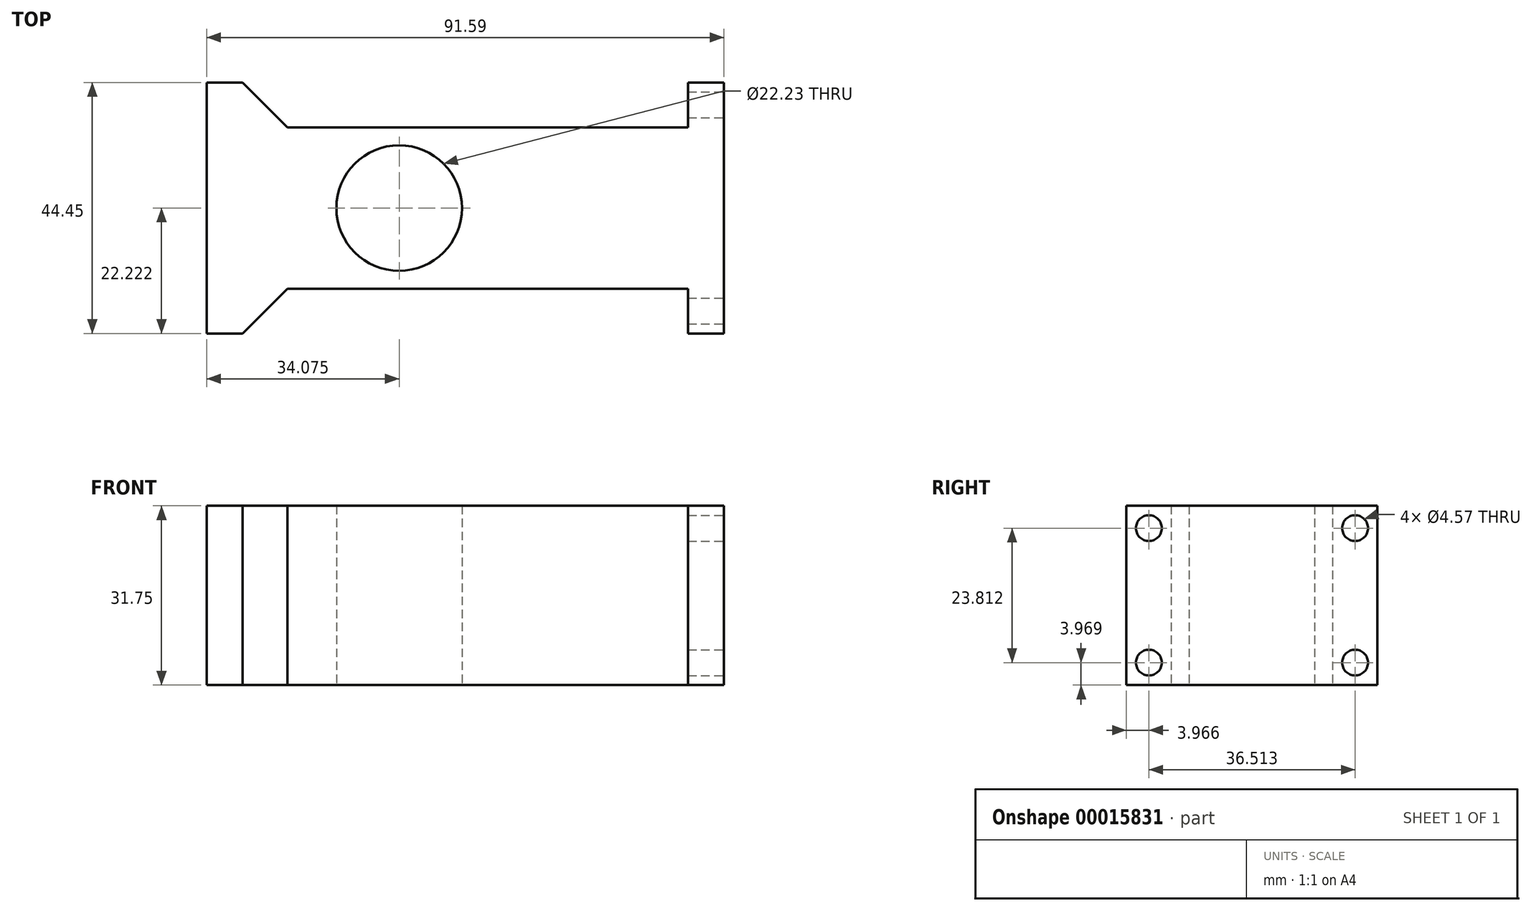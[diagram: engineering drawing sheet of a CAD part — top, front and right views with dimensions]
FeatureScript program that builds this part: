
annotation { "Feature Type Name" : "Feature", "Feature Type Description" : "" }
export const myFeature = defineFeature(function(context is Context, id is Id, definition is map)
    precondition{}
    {
        {
            var Q0;
            Q0=qCreatedBy(makeId("Top.planeOp"),FACE);
            var sketch = newSketch(context, id + "F0", { "sketchPlane" : qUnion([Q0])});
            skLineSegment(sketch, "E0.bottom", {"start": v(0, 0) * mm, "end": v(-78.9, 0) * mm});
            skLineSegment(sketch, "E0.top", {"start": v(0, -28.58) * mm, "end": v(-78.9, -28.58) * mm});
            skLineSegment(sketch, "E1.bottom", {"start": v(0, 0) * mm, "end": v(6.35, 0) * mm, "construction": true});
            skLineSegment(sketch, "E1.top", {"start": v(0, 7.94) * mm, "end": v(6.35, 7.94) * mm});
            skLineSegment(sketch, "E1.left", {"start": v(0, 0) * mm, "end": v(0, 7.94) * mm});
            skLineSegment(sketch, "E1.right", {"start": v(6.35, 0) * mm, "end": v(6.35, 7.94) * mm});
            skLineSegment(sketch, "E2.bottom", {"start": v(0, -28.58) * mm, "end": v(6.35, -28.58) * mm});
            skLineSegment(sketch, "E2.top", {"start": v(0, -36.51) * mm, "end": v(6.35, -36.51) * mm});
            skLineSegment(sketch, "E2.left", {"start": v(0, -28.58) * mm, "end": v(0, -36.51) * mm});
            skLineSegment(sketch, "E2.right", {"start": v(6.35, -28.58) * mm, "end": v(6.35, -36.51) * mm});
            skLineSegment(sketch, "E3", {"start": v(6.35, 0) * mm, "end": v(6.35, -28.58) * mm});
            skCircle(sketch, "E4", {"center": v(-51.16, -14.29) * mm, "radius": 11.11 * mm});
            skLineSegment(sketch, "E5", {"start": v(-51.16, -14.29) * mm, "end": v(-85.24, -14.29) * mm});
            skLineSegment(sketch, "E6.bottom", {"start": v(-78.9, -28.58) * mm, "end": v(-85.24, -28.58) * mm, "construction": true});
            skLineSegment(sketch, "E6.top", {"start": v(-78.9, -36.51) * mm, "end": v(-85.24, -36.51) * mm});
            skLineSegment(sketch, "E6.left", {"start": v(-78.9, -28.58) * mm, "end": v(-78.9, -36.51) * mm});
            skLineSegment(sketch, "E6.right", {"start": v(-85.24, -28.58) * mm, "end": v(-85.24, -36.51) * mm});
            skLineSegment(sketch, "E7.bottom", {"start": v(-78.9, 0) * mm, "end": v(-85.24, 0) * mm, "construction": true});
            skLineSegment(sketch, "E7.top", {"start": v(-78.9, 7.94) * mm, "end": v(-85.24, 7.94) * mm});
            skLineSegment(sketch, "E7.left", {"start": v(-78.9, 0) * mm, "end": v(-78.9, 7.94) * mm});
            skLineSegment(sketch, "E7.right", {"start": v(-85.24, 0) * mm, "end": v(-85.24, 7.94) * mm});
            skLineSegment(sketch, "E8", {"start": v(-85.24, 0) * mm, "end": v(-85.24, -28.58) * mm});
            skSolve(sketch);
        }
        {
            var Q0;
            Q0 = qSketchRegion(id + "F0", true);
            extrude(context, id + "F1", {"entities" : qUnion([Q0]), "depth" : 31.75 * mm});
        }
        {
            var Q0;
            Q0=makeQuery(id+"F1.opExtrude","SWEPT_FACE",FACE,{"disambiguationData":[OSD([sQuery(id+"F0.wireOp",EDGE,"E1.right"),sQuery(id+"F0.wireOp",EDGE,"E2.right"),sQuery(id+"F0.wireOp",EDGE,"E3")])]});
            var sketch = newSketch(context, id + "F2", { "sketchPlane" : qUnion([Q0])});
            skLineSegment(sketch, "E9", {"start": v(-32.54, 31.75) * mm, "end": v(-32.54, 27.78) * mm});
            skLineSegment(sketch, "E10", {"start": v(3.97, 31.75) * mm, "end": v(3.97, 27.78) * mm});
            skLineSegment(sketch, "E11", {"start": v(3.97, 0) * mm, "end": v(3.97, 3.97) * mm});
            skLineSegment(sketch, "E12", {"start": v(-32.54, 0) * mm, "end": v(-32.54, 3.97) * mm});
            skCircle(sketch, "E13", {"center": v(-32.54, 27.78) * mm, "radius": 2.29 * mm});
            skCircle(sketch, "E14", {"center": v(-32.54, 3.97) * mm, "radius": 2.29 * mm});
            skCircle(sketch, "E15", {"center": v(3.97, 3.97) * mm, "radius": 2.29 * mm});
            skCircle(sketch, "E16", {"center": v(3.97, 27.78) * mm, "radius": 2.29 * mm});
            skSolve(sketch);
        }
        {
            var Q0;
            Q0 = qSketchRegion(id + "F2", true);
            var Q1;
            Q1=makeQuery(id+"F1.opExtrude","SWEPT_FACE",FACE,{"disambiguationData":[OSD([sQuery(id+"F0.wireOp",EDGE,"E1.left")])]});
            extrude(context, id + "F3", {"entities" : qUnion([Q0]), "operationType" : NewBodyOperationType.REMOVE, "endBound" : BoundingType.UP_TO_SURFACE, "oppositeDirection" : true, "endBoundEntityFace" : qUnion([Q1]), "depth" : 25.4 * mm});
        }
        {
            var Q0;
            Q0=makeQuery(id+"F1.opExtrude","SWEPT_EDGE",EDGE,{"disambiguationData":[OSD([sQuery(id+"F0.wireOp",EDGE,"E0.bottom"),sQuery(id+"F0.wireOp",EDGE,"E7.left")])]});
            var Q1;
            Q1=makeQuery(id+"F1.opExtrude","SWEPT_EDGE",EDGE,{"disambiguationData":[OSD([sQuery(id+"F0.wireOp",EDGE,"E0.top"),sQuery(id+"F0.wireOp",EDGE,"E6.left")])]});
            chamfer(context, id + "F4", {"entities" : qUnion([Q0, Q1]), "width" : 7.94 * mm, "tangentPropagation" : true});
        }
    });
